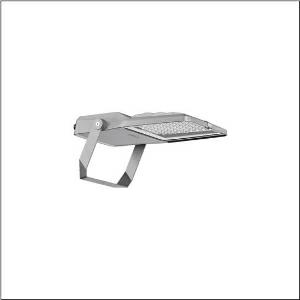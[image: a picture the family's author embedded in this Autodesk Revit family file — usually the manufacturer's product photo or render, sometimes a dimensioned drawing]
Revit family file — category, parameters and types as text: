
# Revit family: floodlight_fl_21_mini___pl43_5xa7775b2a1a_e8ea
name_source: partatom
category: Lighting Fixtures
units: mm (PartAtom-declared; Revit-internal decimal feet)

## family parameters
Cut with Voids When Loaded = No
Host = Face
Light Source = No
Part Type = Normal
Room Calculation Point = No
Round Connector Dimension = Use Diameter
Shared = No

## types (1)
- --- (1 x LED, 6390 lm, 45.7 W, 3000K)
    Apparent Load = 46 VA
    CIE Flux Codes = 27 78 99 100 100
    Color Rendering = 70
    Color Temperature = 3000K
    Default Elevation = 1800 mm
    Description = Floodlight FL 21 mini, floodlight, primary light control with lens, of PMMA, primary optical cover: protective disc, of toughened safety glass, transparent, light distribution: PL43, light emission: direct distribution, installation type: surface-mounted, LED, High Power LED, rated luminous flux: 6.390lm, luminous efficacy: 140lm/W, light colour: 730, colour temperature: 3000K, control gear: Smart Interface (Zhaga), control: flexible luminous flux parameterisation, time-dependent luminous flux control, constant luminous flux control, overheat protection, pre-setting: logarithmic dimming characteristic, with terminal, 6-pole, mains connection: 220..240V, AC, 50/60Hz, start of lifetime: 46W, end of service life: 48W, reduction: 22W, luminaire housing, of diecast aluminium, powder-coated, Siteco® metallic grey (DB 702S), corrosivity category C5 mid according to DIN EN ISO 12944, suitable for swimming pools, chlorine-resistant, sealing non-destructively replaceable, mounting bracket, of steel, galvanised, powder-coated, Siteco® metallic grey (DB 702S), Smart Interface above, protection rating (complete): IP66, insulation class (complete): insulation class II (safety insulation), certification: CE, ENEC, VDE, protection symbol: D, impact resistance: IK08, permissible operating ambient temperature: -40..+40°C, permissible operating ambient temperature for outdoor applications: -40..+50°C, standard: DIN EN 12944, LABS conformity tested according to VDMA 24364:2018-05, packaging unit: 1 piece

Light Distribution: PL43
    Height = 70 mm
    Lamp = 1 x LED
    Lamp Light Flux = 6390 lm
    Lamp Power = 45.7 W
    Lamp count = 1
    Length = 485 mm
    Luminous efficacy = 140 lm/W
    Manufacturer = Siteco
    ModVariant = No
    Model = 5XA7775B2A1A
    Number of Poles = 1
    OnlyDefault = Yes
    Power Factor = 1
    Product Name = Floodlight FL 21 mini | PL43
    Product group = floodlight | pylon annexe
    ProductGroupID = 6200
    Protection Class = Protection class II
    Protection Degree = IP 66
    RLX_Detail_Level = 1
    RLX_Emergency_Light_Flux = 0 lm
    RLX_Emergency_Type = 0
    RLX_Emergency_Type_DB = No
    RlxData = <blob elided: 95917 chars, md5=070774f6>
    Socket = socket
    Standby Power = 0 W
    System Light Flux = 6390 lm
    System Power = 46 W
    Type Comments = factory setting: luminous flux: 100 % | dim-lin: 254 | 463 mA
    Type Image = l_1006845.jpg
    URL = http://relux.com
    VarID = @adj_161326
    Voltage = 0 V
    Weight = 0.00 kg
    Width = 337 mm

## geometry (parser evidence)
native form markers: Blend x4, Sweep x13
no freeform markers — native parametric forms only
